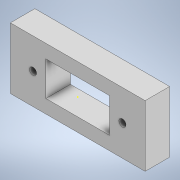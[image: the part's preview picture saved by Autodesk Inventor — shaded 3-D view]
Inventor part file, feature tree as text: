
AUTODESK INVENTOR PART (.ipt)
format: ipt  version: 2022 (Build 260153000, 153)  size: 112,128 bytes
history: native  units: mm
features: sketch x4, extrude x3
ambient origin geometry x8: Origin, YZ Plane, XZ Plane, XY Plane, X Axis, Y Axis, Z Axis, Center Point
bodies: Solid1 (feature_tree)
feature tree (7):
  extrude  "Extrusion1"  Depth=25.0mm
  extrude  "Extrusion2"  Depth=26.0mm
  sketch  "Sketch3"  dims[d5=14.0mm d6=0.0mm d7=0.0mm]
  extrude  "Extrusion3"  TaperAngle=0.0deg  [1 undecoded]
  sketch  "Sketch1"  dims[d0=55.0mm d1=25.0mm]
  sketch  "Sketch2"  dims[d2=10.0mm d3=0.0mm d4=26.0mm]
  sketch  "Sketch4"  dims[d8=2.903mm d9=2.903mm d10=5.25mm d11=5.25mm d12=0.0mm d13=0.0mm]
note: 1 required parameter value undecoded (feature->parameter linkage not recoverable at this tier; creation-order binding heuristic only, values carry confidence <= 0.55)
